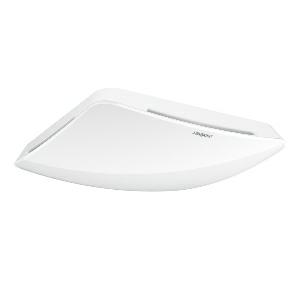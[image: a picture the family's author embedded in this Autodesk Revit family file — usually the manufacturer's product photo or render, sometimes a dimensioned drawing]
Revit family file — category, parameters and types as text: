
# Revit family: multisensor_air_knx_056346
name_source: partatom
category: Elektroinstallationen
revit_build: Autodesk Revit 2016 (Build: 20190508_0715(x64)
units: mm (PartAtom-declared; Revit-internal decimal feet)

## family parameters
Basisbauteil = Fläche
Beim Laden mit Abzugskörper schneiden = Nein
Bemaßung runder Anschluss = Durchmesser verwenden
Beschriftungsausrichtung beibehalten = Nein
Gemeinsam genutzt = Nein
Raumberechnungspunkt = Nein
Teiletyp = Normal

## types (1)
- Multisensor Air KNX
    Apparent Load = 0 VA
    Beschreibung = Type: Other; Dimensions (L x W x H): 33 x 123 x 123 mm; Mains power supply: 30 V; Power consumption: 0,5 W; Sensor Technology: Multisensor; Application, place: Indoors; Application, room: classroom, lecture hall, one-person office, open-plan office, conference room / meeting room, hotel room, care room, duty room, recreation room, sports hall, reception / lobby, Indoors; Installation site: ceiling; Installation: Concealed wiring; Twilight setting TEACH: Yes; Twilight setting: 2 – 1000 lx; Basic light level function: Yes; KNX functions: Comfort, CO2, Light level, HVAC output, Air pressure, Humidity output, Dewpoint, Temperature output, VOC, Photo-cell controller; With bus coupling: Yes; Settings via: ETS software, Bluetooth, Bus; With remote control: No; Interconnection: Yes; IP-rating: IP20; Material: Plastic; Ambient temperature: 0 – 40 °C; Colour: white; Colour, RAL: 9016; Manufacturer's Warranty: 5 years; PU1, EAN: 4007841056346
    Height = 0 mm  [stored 0 ft]
    Hersteller = Steinel
    Length = 33 mm
    ModVariant = Nein
    Modell = 056346
    Mounting Place = Ceiling
    Mounting Type = Recessed
    Number of Poles = 1
    OnlyDefault = Ja
    Power Factor = 1
    Product Name = Multisensor Air KNX
    Product group = Presence detector
    ProductGroupID = 4
    Protection Class = Protection class
    Protection Degree = IP 20
    RlxData = <blob elided: 24817 chars, md5=186efce3>
    SensorDataFile = {"IESDataFiles":[]}
    Typenbild = produkt1_056346.jpg
    Typenkommentare = Product without accessories
    URL = http://relux.com
    VarID = ---
    Voltage = 0 V
    Vorgabe-Ansicht = 1800 mm
    Weight = 0.00 kg
    Width = 123 mm

note: [stored X ft] marks values corroborated as IEEE doubles in the binary element streams (Revit-internal decimal feet)

## geometry (parser evidence)
native form markers: Blend x4, Sweep x13
no freeform markers — native parametric forms only
